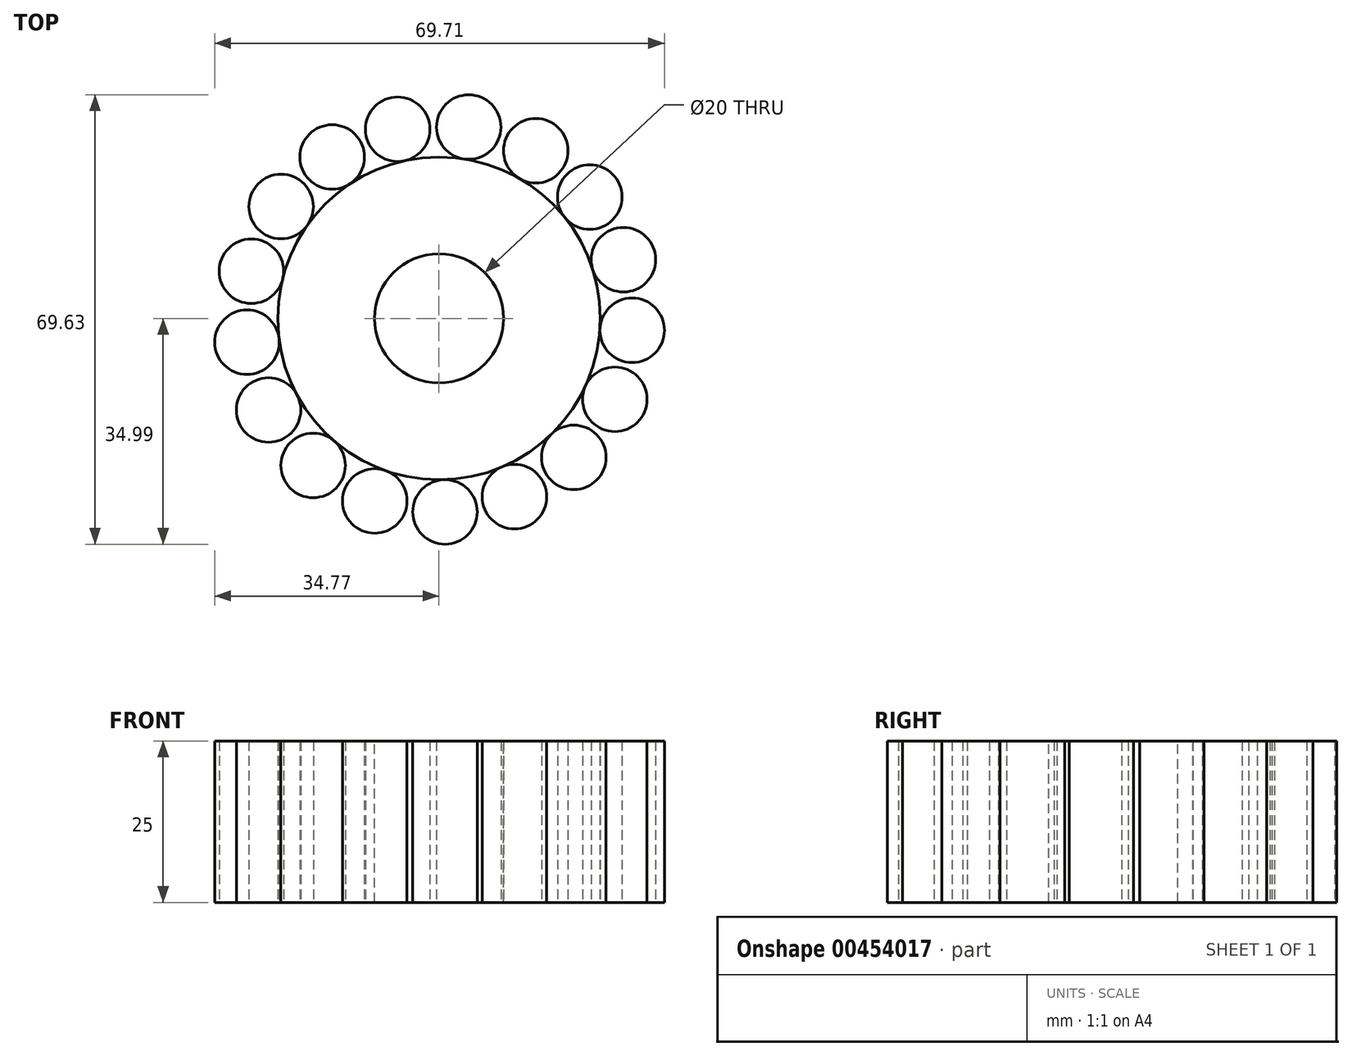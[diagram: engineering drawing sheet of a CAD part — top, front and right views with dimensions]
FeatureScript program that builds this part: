
annotation { "Feature Type Name" : "Feature", "Feature Type Description" : "" }
export const myFeature = defineFeature(function(context is Context, id is Id, definition is map)
    precondition{}
    {
        {
            var Q0;
            Q0=qCreatedBy(makeId("Top.planeOp"),FACE);
            var sketch = newSketch(context, id + "F0", { "sketchPlane" : qUnion([Q0])});
            skCircle(sketch, "E0", {"center": v(0, 0) * mm, "radius": 25 * mm});
            skSolve(sketch);
        }
        {
            var Q0;
            Q0=makeQuery(id+"F0.imprint","IMPRINT",FACE,{"disambiguationData":[TD([[makeQuery(id+"F0.imprint","IMPRINT",EDGE,{"derivedFrom":sQuery(id+"F0.wireOp",EDGE,"E0")}),1.0]])]});
            extrude(context, id + "F1", {"entities" : qUnion([Q0]), "depth" : 25 * mm});
        }
        {
            var Q0;
            Q0=makeQuery(id+"F1.opExtrude","CAP_FACE",FACE,{"disambiguationData":[OSD([sQuery(id+"F0.wireOp",EDGE,"E0")])],"isStart":false});
            var sketch = newSketch(context, id + "F2", { "sketchPlane" : qUnion([Q0])});
            skCircle(sketch, "E1", {"center": v(0, 0) * mm, "radius": 10 * mm});
            skSolve(sketch);
        }
        {
            var Q0;
            Q0=makeQuery(id+"F2.imprint","IMPRINT",FACE,{"disambiguationData":[TD([[makeQuery(id+"F2.imprint","IMPRINT",EDGE,{"derivedFrom":sQuery(id+"F2.wireOp",EDGE,"E1")}),1.0]])]});
            extrude(context, id + "F3", {"entities" : qUnion([Q0]), "operationType" : NewBodyOperationType.REMOVE, "oppositeDirection" : true, "depth" : 25 * mm});
        }
        {
            var Q0;
            Q0=qCreatedBy(makeId("Top.planeOp"),FACE);
            var sketch = newSketch(context, id + "F4", { "sketchPlane" : qUnion([Q0])});
            skCircle(sketch, "E2", {"center": v(15, 25.98) * mm, "radius": 5 * mm});
            skLineSegment(sketch, "E3", {"start": v(0, 0) * mm, "end": v(15, 25.98) * mm, "construction": true});
            skLineSegment(sketch, "E4", {"start": v(0, 0) * mm, "end": v(0, 16.43) * mm, "construction": true});
            skSolve(sketch);
        }
        {
            var Q0;
            Q0 = qSketchRegion(id + "F4", true);
            extrude(context, id + "F5", {"entities" : qUnion([Q0]), "operationType" : NewBodyOperationType.ADD, "depth" : 25 * mm});
        }
        {
            var Q0;
            Q0=makeQuery(id+"F5.opExtrude","SWEPT_BODY",BODY,{"disambiguationData":[OSD([sQuery(id+"F4.wireOp",EDGE,"E2")])]});
            var Q1;
            Q1=makeQuery(id+"F1.opExtrude","SWEPT_FACE",FACE,{"disambiguationData":[OSD([sQuery(id+"F0.wireOp",EDGE,"E0")])]});
            circularPattern(context, id + "F6", {"entities" : qUnion([Q0]), "axis" : qUnion([Q1]), "angle" : 360 * degree, "instanceCount" : 17, "equalSpace" : true});
        }
    });
